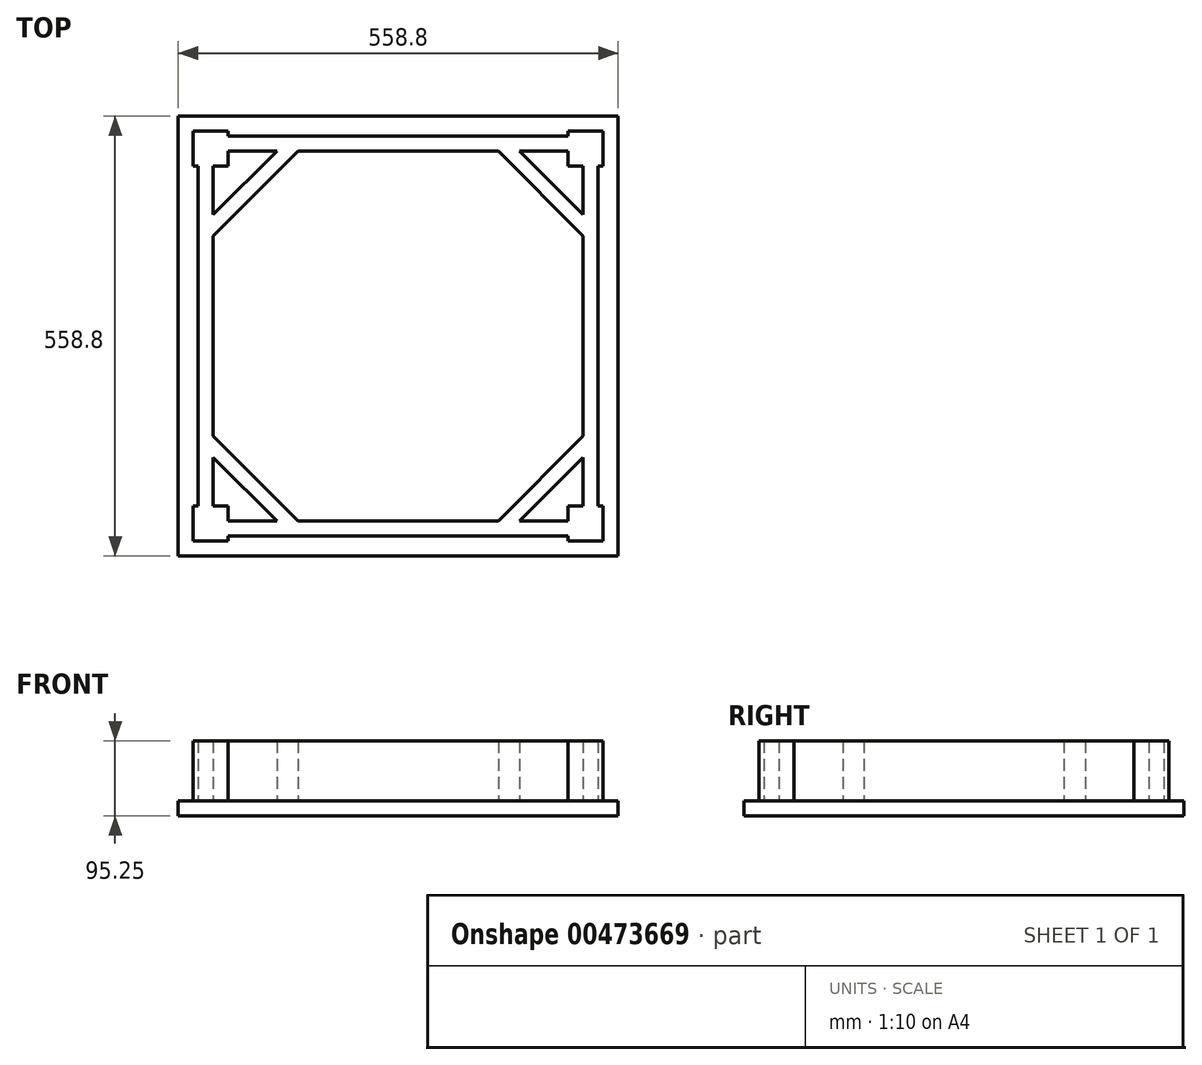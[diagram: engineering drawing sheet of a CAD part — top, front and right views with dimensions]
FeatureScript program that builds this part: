
annotation { "Feature Type Name" : "Feature", "Feature Type Description" : "" }
export const myFeature = defineFeature(function(context is Context, id is Id, definition is map)
    precondition{}
    {
        {
            var Q0;
            Q0=qCreatedBy(makeId("Top.planeOp"),FACE);
            var sketch = newSketch(context, id + "F0", { "sketchPlane" : qUnion([Q0])});
            skLineSegment(sketch, "E0.bottom", {"start": v(0, 0) * mm, "end": v(-279.4, 0) * mm});
            skLineSegment(sketch, "E0.top", {"start": v(0, 558.8) * mm, "end": v(-558.8, 558.8) * mm});
            skLineSegment(sketch, "E0.left", {"start": v(0, 0) * mm, "end": v(0, 558.8) * mm});
            skLineSegment(sketch, "E0.right", {"start": v(-558.8, 0) * mm, "end": v(-558.8, 558.8) * mm});
            skLineSegment(sketch, "E1.0", {"start": v(-63.5, 533.4) * mm, "end": v(-495.3, 533.4) * mm});
            skLineSegment(sketch, "E1.1", {"start": v(-25.4, 63.5) * mm, "end": v(-25.4, 495.3) * mm});
            skLineSegment(sketch, "E1.2", {"start": v(-63.5, 25.4) * mm, "end": v(-495.3, 25.4) * mm});
            skLineSegment(sketch, "E2.0", {"start": v(-63.5, 514.35) * mm, "end": v(-495.3, 514.35) * mm});
            skLineSegment(sketch, "E2.1", {"start": v(-44.45, 63.5) * mm, "end": v(-44.45, 495.3) * mm});
            skLineSegment(sketch, "E2.2", {"start": v(-63.5, 44.45) * mm, "end": v(-495.3, 44.45) * mm});
            skLineSegment(sketch, "E2.3", {"start": v(-514.35, 63.5) * mm, "end": v(-514.35, 495.3) * mm});
            skLineSegment(sketch, "E3.0", {"start": v(-19.05, 539.75) * mm, "end": v(-63.5, 539.75) * mm});
            skLineSegment(sketch, "E3.1", {"start": v(-19.05, 19.05) * mm, "end": v(-19.05, 63.5) * mm});
            skLineSegment(sketch, "E3.2", {"start": v(-19.05, 19.05) * mm, "end": v(-63.5, 19.05) * mm});
            skLineSegment(sketch, "E3.3", {"start": v(-539.75, 19.05) * mm, "end": v(-539.75, 63.5) * mm});
            skLineSegment(sketch, "E4.bottom", {"start": v(-539.75, 19.05) * mm, "end": v(-495.3, 19.05) * mm});
            skLineSegment(sketch, "E4.top", {"start": v(-539.75, 63.5) * mm, "end": v(-495.3, 63.5) * mm});
            skLineSegment(sketch, "E4.right", {"start": v(-495.3, 19.05) * mm, "end": v(-495.3, 63.5) * mm});
            skLineSegment(sketch, "E5.top", {"start": v(-19.05, 63.5) * mm, "end": v(-63.5, 63.5) * mm});
            skLineSegment(sketch, "E5.right", {"start": v(-63.5, 19.05) * mm, "end": v(-63.5, 63.5) * mm});
            skLineSegment(sketch, "E6.top", {"start": v(-19.05, 495.3) * mm, "end": v(-25.4, 495.3) * mm});
            skLineSegment(sketch, "E6.left", {"start": v(-19.05, 539.75) * mm, "end": v(-19.05, 495.3) * mm});
            skLineSegment(sketch, "E6.right", {"start": v(-63.5, 539.75) * mm, "end": v(-63.5, 495.3) * mm});
            skLineSegment(sketch, "E7.bottom", {"start": v(-539.75, 539.75) * mm, "end": v(-495.3, 539.75) * mm});
            skLineSegment(sketch, "E7.top", {"start": v(-539.75, 495.3) * mm, "end": v(-533.4, 495.3) * mm});
            skLineSegment(sketch, "E7.left", {"start": v(-539.75, 539.75) * mm, "end": v(-539.75, 495.3) * mm});
            skLineSegment(sketch, "E7.right", {"start": v(-495.3, 539.75) * mm, "end": v(-495.3, 495.3) * mm});
            skLineSegment(sketch, "E8.trimOffspring", {"start": v(-539.75, 495.3) * mm, "end": v(-539.75, 539.75) * mm});
            skLineSegment(sketch, "E9.trimOffspring", {"start": v(-495.3, 539.75) * mm, "end": v(-539.75, 539.75) * mm});
            skLineSegment(sketch, "E10.trimOffspring", {"start": v(-19.05, 495.3) * mm, "end": v(-19.05, 539.75) * mm});
            skLineSegment(sketch, "E11.trimOffspring", {"start": v(-495.3, 19.05) * mm, "end": v(-539.75, 19.05) * mm});
            skLineSegment(sketch, "E12.0", {"start": v(-533.4, 63.5) * mm, "end": v(-533.4, 495.3) * mm});
            skLineSegment(sketch, "E13.trimOffspring", {"start": v(-514.35, 495.3) * mm, "end": v(-495.3, 495.3) * mm});
            skLineSegment(sketch, "E14", {"start": v(-514.35, 495.3) * mm, "end": v(-533.4, 495.3) * mm});
            skLineSegment(sketch, "E15.bottom", {"start": v(-495.3, 514.35) * mm, "end": v(-406.59, 514.35) * mm});
            skLineSegment(sketch, "E15.left", {"start": v(-514.35, 495.3) * mm, "end": v(-514.35, 406.59) * mm});
            skLineSegment(sketch, "E16", {"start": v(-406.59, 514.35) * mm, "end": v(-514.35, 406.59) * mm});
            skLineSegment(sketch, "E17.0", {"start": v(-433.53, 514.35) * mm, "end": v(-514.35, 433.53) * mm});
            skLineSegment(sketch, "E18.bottom", {"start": v(-495.3, 44.45) * mm, "end": v(-406.59, 44.45) * mm});
            skLineSegment(sketch, "E18.left", {"start": v(-514.35, 63.5) * mm, "end": v(-514.35, 152.21) * mm});
            skLineSegment(sketch, "E19", {"start": v(-406.59, 44.45) * mm, "end": v(-514.35, 152.21) * mm});
            skLineSegment(sketch, "E20.0", {"start": v(-433.53, 44.45) * mm, "end": v(-514.35, 125.27) * mm});
            skLineSegment(sketch, "E21.MirrorCS", {"start": v(-152.21, 514.35) * mm, "end": v(-44.45, 406.59) * mm});
            skLineSegment(sketch, "E22.MirrorCS", {"start": v(-125.27, 514.35) * mm, "end": v(-44.45, 433.53) * mm});
            skLineSegment(sketch, "E23.MirrorCS", {"start": v(-152.21, 44.45) * mm, "end": v(-44.45, 152.21) * mm});
            skLineSegment(sketch, "E24.MirrorCS", {"start": v(-125.27, 44.45) * mm, "end": v(-44.45, 125.27) * mm});
            skPoint(sketch, "E25.end.orphan", {"position": v(-279.4, 0) * mm});
            skPoint(sketch, "E26.orphan", {"position": v(-514.35, 514.35) * mm});
            skPoint(sketch, "E27.orphan", {"position": v(-514.35, 44.45) * mm});
            skLineSegment(sketch, "E28", {"start": v(-514.35, 433.53) * mm, "end": v(-500.88, 420.06) * mm, "construction": true});
            skLineSegment(sketch, "E29.0", {"start": v(-508, 0) * mm, "end": v(-508, 19.05) * mm});
            skLineSegment(sketch, "E30.0", {"start": v(-50.8, 0) * mm, "end": v(-50.8, 19.05) * mm});
            skLineSegment(sketch, "E31.trimOffspring", {"start": v(-50.8, 439.88) * mm, "end": v(-50.8, 495.3) * mm});
            skLineSegment(sketch, "E32.trimOffspring", {"start": v(-50.8, 539.75) * mm, "end": v(-50.8, 558.8) * mm});
            skLineSegment(sketch, "E33.trimOffspring", {"start": v(-50.8, 63.5) * mm, "end": v(-50.8, 118.92) * mm});
            skLineSegment(sketch, "E34.trimOffspring", {"start": v(-50.8, 145.86) * mm, "end": v(-50.8, 412.94) * mm});
            skLineSegment(sketch, "E35.trimOffspring", {"start": v(-508, 63.5) * mm, "end": v(-508, 118.92) * mm});
            skLineSegment(sketch, "E36.trimOffspring", {"start": v(-508, 145.86) * mm, "end": v(-508, 412.94) * mm});
            skLineSegment(sketch, "E37.trimOffspring", {"start": v(-508, 439.88) * mm, "end": v(-508, 495.3) * mm});
            skLineSegment(sketch, "E38.trimOffspring", {"start": v(-508, 539.75) * mm, "end": v(-508, 558.8) * mm});
            skLineSegment(sketch, "E39.trimOffspring", {"start": v(-508, 0) * mm, "end": v(-558.8, 0) * mm});
            skLineSegment(sketch, "E40", {"start": v(-508, 0) * mm, "end": v(-279.4, 0) * mm});
            skLineSegment(sketch, "E41.bottom", {"start": v(0, -76.23) * mm, "end": v(-558.8, -76.23) * mm});
            skLineSegment(sketch, "E41.top", {"start": v(-50.8, -57.18) * mm, "end": v(-558.8, -57.18) * mm});
            skLineSegment(sketch, "E41.left", {"start": v(0, -76.23) * mm, "end": v(0, -57.18) * mm});
            skLineSegment(sketch, "E41.right", {"start": v(-558.8, -76.23) * mm, "end": v(-558.8, -57.18) * mm});
            skLineSegment(sketch, "E42.trimOffspring", {"start": v(-539.75, -76.23) * mm, "end": v(-539.75, -152.43) * mm});
            skLineSegment(sketch, "E43.trimOffspring", {"start": v(-63.5, -76.23) * mm, "end": v(-63.5, -152.43) * mm});
            skLineSegment(sketch, "E44.trimOffspring", {"start": v(-19.05, -76.23) * mm, "end": v(-19.05, -838.23) * mm});
            skLineSegment(sketch, "E45.bottom", {"start": v(-495.3, -76.23) * mm, "end": v(-63.5, -76.23) * mm});
            skLineSegment(sketch, "E45.top", {"start": v(-495.3, -152.43) * mm, "end": v(-63.5, -152.43) * mm});
            skLineSegment(sketch, "E45.left", {"start": v(-495.3, -76.23) * mm, "end": v(-495.3, -152.43) * mm});
            skLineSegment(sketch, "E46", {"start": v(-539.75, -838.23) * mm, "end": v(-508, -838.23) * mm});
            skLineSegment(sketch, "E47", {"start": v(-508, -838.23) * mm, "end": v(-495.3, -152.43) * mm});
            skLineSegment(sketch, "E48.MirrorCS", {"start": v(-50.8, -838.23) * mm, "end": v(-63.5, -152.43) * mm});
            skLineSegment(sketch, "E49.MirrorCS", {"start": v(-19.05, -838.23) * mm, "end": v(-50.8, -838.23) * mm});
            skLineSegment(sketch, "E50.0", {"start": v(-508, -76.23) * mm, "end": v(-508, -57.18) * mm});
            skLineSegment(sketch, "E51.0", {"start": v(-50.8, -76.23) * mm, "end": v(-50.8, -57.18) * mm});
            skLineSegment(sketch, "E52", {"start": v(-50.8, 558.8) * mm, "end": v(-508, 558.8) * mm});
            skLineSegment(sketch, "E53.left", {"start": v(0, -57.18) * mm, "end": v(0, -76.35) * mm});
            skLineSegment(sketch, "E54.MirrorCS", {"start": v(95.18, -76.23) * mm, "end": v(95.18, -838.23) * mm});
            skLineSegment(sketch, "E55.MirrorCS", {"start": v(126.93, -838.23) * mm, "end": v(139.63, -152.43) * mm});
            skLineSegment(sketch, "E56.MirrorCS", {"start": v(571.43, -152.43) * mm, "end": v(139.63, -152.43) * mm});
            skLineSegment(sketch, "E57.MirrorCS", {"start": v(584.13, -838.23) * mm, "end": v(571.43, -152.43) * mm});
            skLineSegment(sketch, "E58.MirrorCS", {"start": v(571.43, -76.23) * mm, "end": v(571.43, -152.43) * mm});
            skLineSegment(sketch, "E59.MirrorCS", {"start": v(615.88, -76.23) * mm, "end": v(615.88, -838.23) * mm});
            skLineSegment(sketch, "E60.MirrorCS", {"start": v(571.43, -76.23) * mm, "end": v(139.63, -76.23) * mm});
            skLineSegment(sketch, "E61.MirrorCS", {"start": v(76.13, -57.18) * mm, "end": v(634.93, -57.18) * mm});
            skLineSegment(sketch, "E62.MirrorCS", {"start": v(139.63, -76.23) * mm, "end": v(139.63, -152.43) * mm});
            skLineSegment(sketch, "E63.MirrorCS", {"start": v(76.13, -76.23) * mm, "end": v(634.93, -76.23) * mm});
            skLineSegment(sketch, "E64.MirrorCS", {"start": v(76.13, -76.23) * mm, "end": v(76.13, -57.18) * mm});
            skLineSegment(sketch, "E65.MirrorCS", {"start": v(634.93, -76.23) * mm, "end": v(634.93, -57.18) * mm});
            skLineSegment(sketch, "E66.MirrorCS", {"start": v(95.18, -838.23) * mm, "end": v(126.93, -838.23) * mm});
            skLineSegment(sketch, "E67.MirrorCS", {"start": v(615.88, -838.23) * mm, "end": v(584.13, -838.23) * mm});
            skLineSegment(sketch, "E68", {"start": v(-514.35, -152.43) * mm, "end": v(-533.4, -152.43) * mm, "construction": true});
            skLineSegment(sketch, "E69", {"start": v(-539.75, -152.43) * mm, "end": v(-539.75, -76.23) * mm});
            skLineSegment(sketch, "E70.0", {"start": v(-533.4, -152.43) * mm, "end": v(-533.4, -76.23) * mm, "construction": true});
            skLineSegment(sketch, "E71.0", {"start": v(-514.35, -76.23) * mm, "end": v(-514.35, -152.43) * mm, "construction": true});
            skLineSegment(sketch, "E72", {"start": v(-508, 19.05) * mm, "end": v(-508, 63.5) * mm, "construction": true});
            skLineSegment(sketch, "E73", {"start": v(-508, 495.3) * mm, "end": v(-508, 539.75) * mm, "construction": true});
            skLineSegment(sketch, "E74", {"start": v(-50.8, 495.3) * mm, "end": v(-50.8, 539.75) * mm, "construction": true});
            skLineSegment(sketch, "E75", {"start": v(-50.8, 19.05) * mm, "end": v(-50.8, 63.5) * mm, "construction": true});
            skLineSegment(sketch, "E76", {"start": v(-50.8, 118.92) * mm, "end": v(-50.8, 145.86) * mm, "construction": true});
            skLineSegment(sketch, "E77", {"start": v(-50.8, 439.88) * mm, "end": v(-50.8, 412.94) * mm, "construction": true});
            skLineSegment(sketch, "E78", {"start": v(-508, 439.88) * mm, "end": v(-508, 412.94) * mm, "construction": true});
            skLineSegment(sketch, "E79", {"start": v(-508, 145.86) * mm, "end": v(-508, 118.92) * mm, "construction": true});
            skLineSegment(sketch, "E80.MirrorCS", {"start": v(-44.45, -76.23) * mm, "end": v(-44.45, -152.43) * mm, "construction": true});
            skLineSegment(sketch, "E81.MirrorCS", {"start": v(-25.4, -152.43) * mm, "end": v(-25.4, -76.23) * mm, "construction": true});
            skLineSegment(sketch, "E82.MirrorCS", {"start": v(-44.45, -152.43) * mm, "end": v(-25.4, -152.43) * mm, "construction": true});
            skLineSegment(sketch, "E83.left", {"start": v(0, -57.18) * mm, "end": v(0, -76.23) * mm});
            skLineSegment(sketch, "E83.right", {"start": v(76.13, -57.18) * mm, "end": v(76.13, -76.23) * mm});
            skLineSegment(sketch, "E84", {"start": v(38.07, -57.18) * mm, "end": v(38.07, -169.64) * mm, "construction": true});
            skLineSegment(sketch, "E85.MirrorCS", {"start": v(101.53, -152.43) * mm, "end": v(101.53, -76.23) * mm, "construction": true});
            skLineSegment(sketch, "E86.MirrorCS", {"start": v(120.58, -76.23) * mm, "end": v(120.58, -152.43) * mm, "construction": true});
            skLineSegment(sketch, "E87.MirrorCS", {"start": v(120.58, -152.43) * mm, "end": v(101.53, -152.43) * mm, "construction": true});
            skLineSegment(sketch, "E88.MirrorCS", {"start": v(609.53, -152.43) * mm, "end": v(609.53, -76.23) * mm, "construction": true});
            skLineSegment(sketch, "E89.MirrorCS", {"start": v(590.48, -152.43) * mm, "end": v(609.53, -152.43) * mm, "construction": true});
            skLineSegment(sketch, "E90.MirrorCS", {"start": v(590.48, -76.23) * mm, "end": v(590.48, -152.43) * mm, "construction": true});
            skLineSegment(sketch, "E91.trimOffspring", {"start": v(-125.27, -76.23) * mm, "end": v(-125.27, -152.43) * mm, "construction": true});
            skLineSegment(sketch, "E92.trimOffspring", {"start": v(-152.21, -76.23) * mm, "end": v(-152.21, -152.43) * mm, "construction": true});
            skLineSegment(sketch, "E93.trimOffspring", {"start": v(-406.59, -76.23) * mm, "end": v(-406.59, -152.43) * mm, "construction": true});
            skLineSegment(sketch, "E94.trimOffspring", {"start": v(-433.53, -76.23) * mm, "end": v(-433.53, -152.43) * mm, "construction": true});
            skLineSegment(sketch, "E95", {"start": v(-63.5, 44.45) * mm, "end": v(-63.5, 25.4) * mm});
            skLineSegment(sketch, "E96.trimOffspring", {"start": v(-44.45, 495.3) * mm, "end": v(-63.5, 495.3) * mm});
            skLineSegment(sketch, "E97", {"start": v(-44.45, 495.3) * mm, "end": v(-25.4, 495.3) * mm});
            skLineSegment(sketch, "E98", {"start": v(-50.8, -57.18) * mm, "end": v(0, -57.18) * mm});
            skLineSegment(sketch, "E99", {"start": v(-25.4, 279.4) * mm, "end": v(0, 279.4) * mm, "construction": true});
            skLineSegment(sketch, "E100.MirrorCS", {"start": v(201.4, -76.23) * mm, "end": v(201.4, -152.43) * mm, "construction": true});
            skLineSegment(sketch, "E101.MirrorCS", {"start": v(228.35, -76.23) * mm, "end": v(228.35, -152.43) * mm, "construction": true});
            skLineSegment(sketch, "E102.MirrorCS", {"start": v(509.66, -76.23) * mm, "end": v(509.66, -152.43) * mm, "construction": true});
            skLineSegment(sketch, "E103.MirrorCS", {"start": v(482.72, -76.23) * mm, "end": v(482.72, -152.43) * mm, "construction": true});
            skLineSegment(sketch, "E104.bottom", {"start": v(-495.3, -152.43) * mm, "end": v(-384.94, -152.43) * mm});
            skLineSegment(sketch, "E105.trimOffspring", {"start": v(-501.89, -508.03) * mm, "end": v(-56.91, -508.03) * mm});
            skLineSegment(sketch, "E106.trimOffspring", {"start": v(-502.36, -533.43) * mm, "end": v(-56.44, -533.43) * mm});
            skPoint(sketch, "E104.left.end.orphan", {"position": v(-495.3, -508.03) * mm});
            skLineSegment(sketch, "E107", {"start": v(-501.89, -508.03) * mm, "end": v(-539.75, -508.03) * mm, "construction": true});
            skLineSegment(sketch, "E108.trimOffspring", {"start": v(-539.75, -508.03) * mm, "end": v(-539.75, -838.23) * mm});
            skLineSegment(sketch, "E109", {"start": v(-539.75, -508.03) * mm, "end": v(-539.75, -152.43) * mm});
            skSolve(sketch);
        }
        {
            var Q0;
            Q0=qCreatedBy(makeId("Top.planeOp"),FACE);
            var sketch = newSketch(context, id + "F1", { "sketchPlane" : qUnion([Q0])});
            skLineSegment(sketch, "E110.bottom", {"start": v(0, 0) * mm, "end": v(-558.8, 0) * mm});
            skLineSegment(sketch, "E110.top", {"start": v(0, 558.8) * mm, "end": v(-558.8, 558.8) * mm});
            skLineSegment(sketch, "E110.left", {"start": v(0, 0) * mm, "end": v(0, 558.8) * mm});
            skLineSegment(sketch, "E110.right", {"start": v(-558.8, 0) * mm, "end": v(-558.8, 558.8) * mm});
            skSolve(sketch);
        }
        {
            var Q0;
            Q0=makeQuery(id+"F1.imprint","IMPRINT",FACE,{"disambiguationData":[TD([[makeQuery(id+"F1.imprint","IMPRINT",EDGE,{"derivedFrom":sQuery(id+"F1.wireOp",EDGE,"E110.bottom")}),-1.0]])]});
            extrude(context, id + "F2", {"entities" : qUnion([Q0]), "oppositeDirection" : true, "depth" : 19.05 * mm});
        }
        {
            var Q0;
            Q0=makeQuery(id+"F0.imprint","IMPRINT",FACE,{"disambiguationData":[TD([[makeQuery(id+"F0.imprint","IMPRINT",EDGE,{"derivedFrom":sQuery(id+"F0.wireOp",EDGE,"E7.top")}),1.0]])]});
            var Q1;
            {var subQ6=sQuery(id+"F0.wireOp",EDGE,"E3.3");Q1=makeQuery(id+"F0.imprint","IMPRINT",FACE,{"disambiguationData":[TD([[makeQuery(id+"F0.imprint","IMPRINT",EDGE,{"derivedFrom":subQ6}),-1.0]])]});}
            var Q2;
            {var subQ3=sQuery(id+"F0.wireOp",EDGE,"E3.1");Q2=makeQuery(id+"F0.imprint","IMPRINT",FACE,{"disambiguationData":[TD([[makeQuery(id+"F0.imprint","IMPRINT",EDGE,{"derivedFrom":subQ3}),1.0]])]});}
            var Q3;
            Q3=makeQuery(id+"F0.imprint","IMPRINT",FACE,{"disambiguationData":[TD([[makeQuery(id+"F0.imprint","IMPRINT",EDGE,{"derivedFrom":sQuery(id+"F0.wireOp",EDGE,"E6.top")}),-1.0]])]});
            var Q4;
            {var subQ6=sQuery(id+"F0.wireOp",EDGE,"E1.1");Q4=makeQuery(id+"F0.imprint","IMPRINT",FACE,{"disambiguationData":[TD([[makeQuery(id+"F0.imprint","IMPRINT",EDGE,{"derivedFrom":subQ6}),1.0]])]});}
            var Q5;
            {var subQ5=sQuery(id+"F0.wireOp",EDGE,"E1.0");Q5=makeQuery(id+"F0.imprint","IMPRINT",FACE,{"disambiguationData":[TD([[makeQuery(id+"F0.imprint","IMPRINT",EDGE,{"derivedFrom":subQ5}),1.0]])]});}
            var Q6;
            {var subQ6=sQuery(id+"F0.wireOp",EDGE,"E2.3");Q6=makeQuery(id+"F0.imprint","IMPRINT",FACE,{"disambiguationData":[TD([[makeQuery(id+"F0.imprint","IMPRINT",EDGE,{"derivedFrom":subQ6}),1.0]])]});}
            var Q7;
            {var subQ4=sQuery(id+"F0.wireOp",EDGE,"E15.bottom");var subQ6=sQuery(id+"F0.wireOp",EDGE,"E17.0");var subQ8=makeQuery(id+"F0.imprint","INTERSECT",VERTEX,{"derivedFrom":[subQ4,subQ6]});Q7=makeQuery(id+"F0.imprint","IMPRINT",FACE,{"disambiguationData":[TD([[makeQuery(id+"F0.imprint","IMPRINT",EDGE,{"disambiguationData":[TD([[subQ8,-1.0]])],"derivedFrom":subQ6}),1.0]])]});}
            var Q8;
            {var subQ4=sQuery(id+"F0.wireOp",EDGE,"E18.bottom");var subQ6=sQuery(id+"F0.wireOp",EDGE,"E20.0");var subQ8=makeQuery(id+"F0.imprint","INTERSECT",VERTEX,{"derivedFrom":[subQ4,subQ6]});Q8=makeQuery(id+"F0.imprint","IMPRINT",FACE,{"disambiguationData":[TD([[makeQuery(id+"F0.imprint","IMPRINT",EDGE,{"disambiguationData":[TD([[subQ8,-1.0]])],"derivedFrom":subQ6}),-1.0]])]});}
            var Q9;
            {var subQ0=sQuery(id+"F0.wireOp",EDGE,"E23.MirrorCS");var subQ1=sQuery(id+"F0.wireOp",EDGE,"E2.1");var subQ2=makeQuery(id+"F0.imprint","INTERSECT",VERTEX,{"derivedFrom":[subQ1,subQ0]});Q9=makeQuery(id+"F0.imprint","IMPRINT",FACE,{"disambiguationData":[TD([[makeQuery(id+"F0.imprint","IMPRINT",EDGE,{"disambiguationData":[TD([[subQ2,1.0]])],"derivedFrom":subQ1}),1.0]])]});}
            var Q10;
            {var subQ4=sQuery(id+"F0.wireOp",EDGE,"E1.2");Q10=makeQuery(id+"F0.imprint","IMPRINT",FACE,{"disambiguationData":[TD([[makeQuery(id+"F0.imprint","IMPRINT",EDGE,{"derivedFrom":subQ4}),-1.0]])]});}
            var Q11;
            {var subQ0=sQuery(id+"F0.wireOp",EDGE,"E21.MirrorCS");var subQ1=sQuery(id+"F0.wireOp",EDGE,"E2.0");var subQ2=makeQuery(id+"F0.imprint","INTERSECT",VERTEX,{"derivedFrom":[subQ1,subQ0]});Q11=makeQuery(id+"F0.imprint","IMPRINT",FACE,{"disambiguationData":[TD([[makeQuery(id+"F0.imprint","IMPRINT",EDGE,{"disambiguationData":[TD([[subQ2,1.0]])],"derivedFrom":subQ1}),1.0]])]});}
            extrude(context, id + "F3", {"entities" : qUnion([Q0, Q1, Q2, Q3, Q4, Q5, Q6, Q7, Q8, Q9, Q10, Q11]), "operationType" : NewBodyOperationType.ADD, "depth" : 76.2 * mm});
        }
    });
